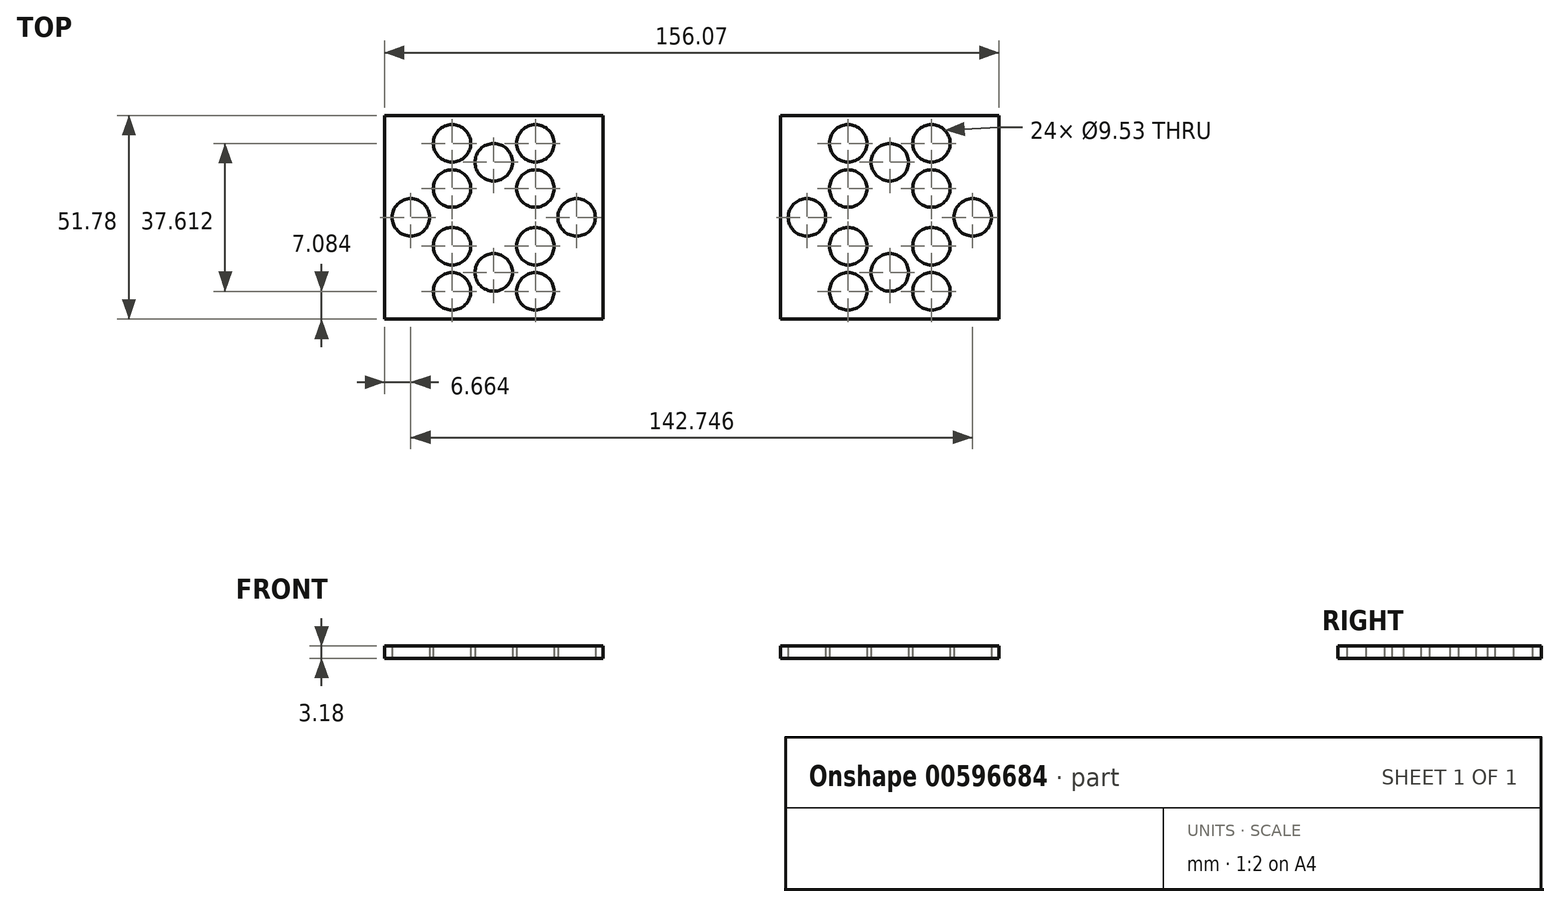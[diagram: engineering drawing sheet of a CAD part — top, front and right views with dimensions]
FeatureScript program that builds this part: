
annotation { "Feature Type Name" : "Feature", "Feature Type Description" : "" }
export const myFeature = defineFeature(function(context is Context, id is Id, definition is map)
    precondition{}
    {
        {
            var Q0;
            Q0=qCreatedBy(makeId("Top.planeOp"),FACE);
            var sketch = newSketch(context, id + "F0", { "sketchPlane" : qUnion([Q0])});
            skCircle(sketch, "E0", {"center": v(27.72, 39.89) * mm, "radius": 4.76 * mm});
            skLineSegment(sketch, "E1.bottom", {"start": v(0, 0) * mm, "end": v(55.44, 0) * mm});
            skLineSegment(sketch, "E1.top", {"start": v(0, 51.78) * mm, "end": v(55.44, 51.78) * mm});
            skLineSegment(sketch, "E1.left", {"start": v(0, 0) * mm, "end": v(0, 51.78) * mm});
            skLineSegment(sketch, "E1.right", {"start": v(55.44, 0) * mm, "end": v(55.44, 51.78) * mm});
            skLineSegment(sketch, "E2", {"start": v(0, 51.78) * mm, "end": v(17.14, 51.78) * mm});
            skLineSegment(sketch, "E3", {"start": v(55.44, 51.78) * mm, "end": v(38.3, 51.78) * mm});
            skCircle(sketch, "E4", {"center": v(17.14, 44.7) * mm, "radius": 4.76 * mm});
            skCircle(sketch, "E5", {"center": v(17.14, 33.22) * mm, "radius": 4.76 * mm});
            skCircle(sketch, "E6", {"center": v(6.66, 25.9) * mm, "radius": 4.76 * mm});
            skCircle(sketch, "E7.MirrorC", {"center": v(48.78, 25.9) * mm, "radius": 4.76 * mm});
            skCircle(sketch, "E8.MirrorC", {"center": v(38.3, 33.22) * mm, "radius": 4.76 * mm});
            skCircle(sketch, "E9.MirrorC", {"center": v(38.3, 44.7) * mm, "radius": 4.76 * mm});
            skCircle(sketch, "E10.MirrorC", {"center": v(17.14, 18.56) * mm, "radius": 4.76 * mm});
            skCircle(sketch, "E11.MirrorC", {"center": v(27.72, 11.9) * mm, "radius": 4.76 * mm});
            skCircle(sketch, "E12.MirrorC", {"center": v(38.3, 7.08) * mm, "radius": 4.76 * mm});
            skCircle(sketch, "E13.MirrorC", {"center": v(17.14, 7.08) * mm, "radius": 4.76 * mm});
            skCircle(sketch, "E14.MirrorC", {"center": v(38.3, 18.56) * mm, "radius": 4.76 * mm});
            skLineSegment(sketch, "E15.MirrorCS", {"start": v(-45.19, 0) * mm, "end": v(-100.63, 0) * mm});
            skLineSegment(sketch, "E16.MirrorCS", {"start": v(-45.19, 0) * mm, "end": v(-45.19, 51.78) * mm});
            skCircle(sketch, "E17.MirrorC", {"center": v(-93.97, 25.9) * mm, "radius": 4.76 * mm});
            skCircle(sketch, "E18.MirrorC", {"center": v(-51.85, 25.9) * mm, "radius": 4.76 * mm});
            skCircle(sketch, "E19.MirrorC", {"center": v(-83.49, 33.22) * mm, "radius": 4.76 * mm});
            skCircle(sketch, "E20.MirrorC", {"center": v(-62.33, 7.08) * mm, "radius": 4.76 * mm});
            skCircle(sketch, "E21.MirrorC", {"center": v(-83.49, 7.08) * mm, "radius": 4.76 * mm});
            skCircle(sketch, "E22.MirrorC", {"center": v(-72.9, 39.89) * mm, "radius": 4.76 * mm});
            skCircle(sketch, "E23.MirrorC", {"center": v(-62.33, 44.7) * mm, "radius": 4.76 * mm});
            skLineSegment(sketch, "E24.MirrorCS", {"start": v(-100.63, 51.78) * mm, "end": v(-83.49, 51.78) * mm});
            skCircle(sketch, "E25.MirrorC", {"center": v(-72.9, 11.9) * mm, "radius": 4.76 * mm});
            skCircle(sketch, "E26.MirrorC", {"center": v(-83.49, 44.7) * mm, "radius": 4.76 * mm});
            skCircle(sketch, "E27.MirrorC", {"center": v(-62.33, 18.56) * mm, "radius": 4.76 * mm});
            skLineSegment(sketch, "E28.MirrorCS", {"start": v(-100.63, 0) * mm, "end": v(-100.63, 51.78) * mm});
            skCircle(sketch, "E29.MirrorC", {"center": v(-62.33, 33.22) * mm, "radius": 4.76 * mm});
            skLineSegment(sketch, "E30.MirrorCS", {"start": v(-45.19, 51.78) * mm, "end": v(-100.63, 51.78) * mm});
            skCircle(sketch, "E31.MirrorC", {"center": v(-83.49, 18.56) * mm, "radius": 4.76 * mm});
            skLineSegment(sketch, "E32.MirrorCS", {"start": v(-45.19, 51.78) * mm, "end": v(-62.33, 51.78) * mm});
            skSolve(sketch);
        }
        {
            var Q0;
            Q0=makeQuery(id+"F0.imprint","IMPRINT",FACE,{"disambiguationData":[TD([[makeQuery(id+"F0.imprint","IMPRINT",EDGE,{"derivedFrom":sQuery(id+"F0.wireOp",EDGE,"E15.MirrorCS")}),-1.0]])]});
            var Q1;
            Q1=makeQuery(id+"F0.imprint","IMPRINT",FACE,{"disambiguationData":[TD([[makeQuery(id+"F0.imprint","IMPRINT",EDGE,{"derivedFrom":sQuery(id+"F0.wireOp",EDGE,"E0")}),-1.0]])]});
            extrude(context, id + "F1", {"entities" : qUnion([Q0, Q1]), "depth" : 3.17 * mm, "offsetDistance" : 25.4 * mm});
        }
    });
